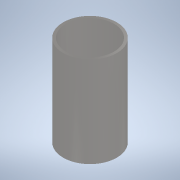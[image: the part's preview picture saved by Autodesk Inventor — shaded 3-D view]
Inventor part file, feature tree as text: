
AUTODESK INVENTOR PART (.ipt)
format: ipt  version: 2022 (Build 260153000, 153)  size: 96,256 bytes
history: native  units: in
note: dims shown in document units (in); Inventor stores cm internally (conversion verified against a paired STEP export)
features: extrude x1, sketch x1
ambient origin geometry x8: Origin, YZ Plane, XZ Plane, XY Plane, X Axis, Y Axis, Z Axis, Center Point
bodies: Solid1 (feature_tree)
feature tree (2):
  extrude  "Extrusion1"  Depth=1.0in
  sketch  "Sketch1"  dims[d0=0.5906in d1=0.0295in d2=1.0in d3=0.0in]
